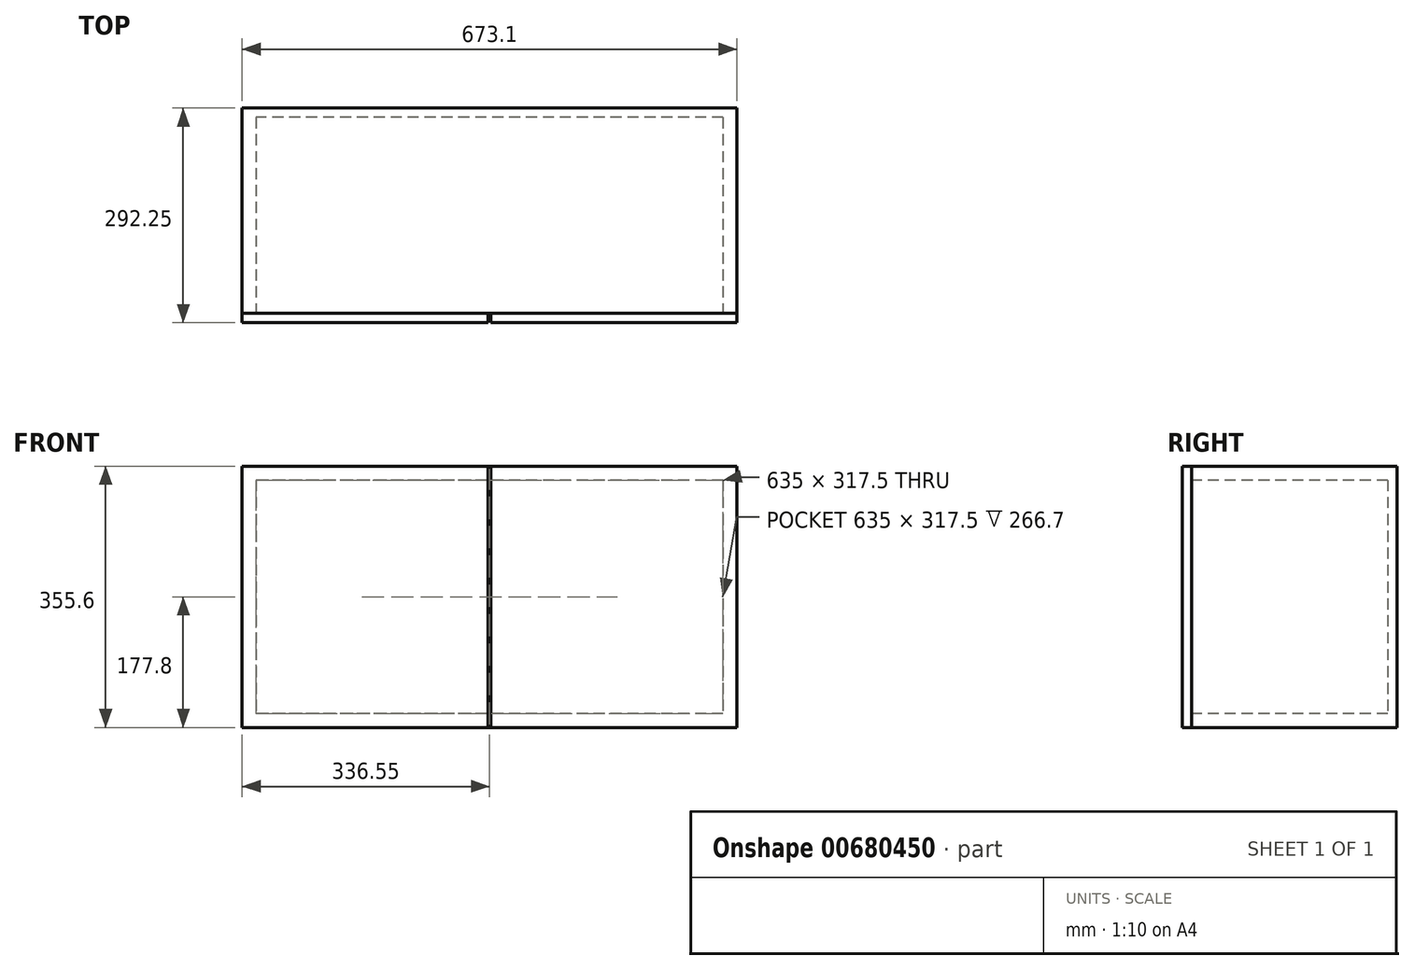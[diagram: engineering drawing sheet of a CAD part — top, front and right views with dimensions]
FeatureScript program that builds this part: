
annotation { "Feature Type Name" : "Feature", "Feature Type Description" : "" }
export const myFeature = defineFeature(function(context is Context, id is Id, definition is map)
    precondition{}
    {
        {
            var Q0;
            Q0=qCreatedBy(makeId("Front.planeOp"),FACE);
            var sketch = newSketch(context, id + "F0", { "sketchPlane" : qUnion([Q0])});
            skLineSegment(sketch, "E0.bottom", {"start": v(-336.55, 177.8) * mm, "end": v(336.55, 177.8) * mm});
            skLineSegment(sketch, "E0.top", {"start": v(-336.55, -177.8) * mm, "end": v(336.55, -177.8) * mm});
            skLineSegment(sketch, "E0.left", {"start": v(-336.55, 177.8) * mm, "end": v(-336.55, -177.8) * mm});
            skLineSegment(sketch, "E0.right", {"start": v(336.55, 177.8) * mm, "end": v(336.55, -177.8) * mm});
            skPoint(sketch, "E0.middle", {"position": v(0, 0) * mm});
            skSolve(sketch);
        }
        {
            var Q0;
            Q0=makeQuery(id+"F0.imprint","IMPRINT",FACE,{"disambiguationData":[TD([[makeQuery(id+"F0.imprint","IMPRINT",EDGE,{"derivedFrom":sQuery(id+"F0.wireOp",EDGE,"E0.bottom")}),-1.0]])]});
            extrude(context, id + "F1", {"entities" : qUnion([Q0]), "endBound" : BoundingType.SYMMETRIC, "depth" : 279.4 * mm});
        }
        {
            var Q0;
            Q0=makeQuery(id+"F1.opExtrude","CAP_FACE",FACE,{"disambiguationData":[OSD([sQuery(id+"F0.wireOp",EDGE,"E0.bottom"),sQuery(id+"F0.wireOp",EDGE,"E0.top"),sQuery(id+"F0.wireOp",EDGE,"E0.left"),sQuery(id+"F0.wireOp",EDGE,"E0.right")])],"isStart":false});
            var sketch = newSketch(context, id + "F2", { "sketchPlane" : qUnion([Q0])});
            skLineSegment(sketch, "E1.bottom", {"start": v(317.5, 158.75) * mm, "end": v(-317.5, 158.75) * mm});
            skLineSegment(sketch, "E1.top", {"start": v(317.5, -158.75) * mm, "end": v(-317.5, -158.75) * mm});
            skLineSegment(sketch, "E1.left", {"start": v(317.5, 158.75) * mm, "end": v(317.5, -158.75) * mm});
            skLineSegment(sketch, "E1.right", {"start": v(-317.5, 158.75) * mm, "end": v(-317.5, -158.75) * mm});
            skPoint(sketch, "E1.middle", {"position": v(0, 0) * mm});
            skSolve(sketch);
        }
        {
            var Q0;
            Q0=qSketchRegion(id+"F2",true);
            var Q1;
            Q1=makeQuery(id+"F1.opExtrude","CAP_FACE",FACE,{"disambiguationData":[OSD([sQuery(id+"F0.wireOp",EDGE,"E0.bottom"),sQuery(id+"F0.wireOp",EDGE,"E0.top"),sQuery(id+"F0.wireOp",EDGE,"E0.left"),sQuery(id+"F0.wireOp",EDGE,"E0.right")])],"isStart":true});
            extrude(context, id + "F3", {"entities" : qUnion([Q0]), "operationType" : NewBodyOperationType.REMOVE, "oppositeDirection" : true, "endBoundEntityFace" : qUnion([Q1]), "depth" : 266.7 * mm});
        }
        {
            var Q0;
            Q0=makeQuery(id+"F1.opExtrude","CAP_FACE",FACE,{"disambiguationData":[OSD([sQuery(id+"F0.wireOp",EDGE,"E0.bottom"),sQuery(id+"F0.wireOp",EDGE,"E0.top"),sQuery(id+"F0.wireOp",EDGE,"E0.left"),sQuery(id+"F0.wireOp",EDGE,"E0.right")])],"isStart":false});
            cPlane(context, id + "F4", {"entities" : qUnion([Q0]), "cplaneType" : CPlaneType.OFFSET, "offset" : .15 * mm, "width" : 150 * mm, "height" : 150 * mm});
        }
        {
            var Q0;
            Q0=qCreatedBy(id+"F4.planeOp",FACE);
            var sketch = newSketch(context, id + "F5", { "sketchPlane" : qUnion([Q0])});
            skLineSegment(sketch, "E2.bottom", {"start": v(-336.55, -177.8) * mm, "end": v(-1.9, -177.8) * mm});
            skLineSegment(sketch, "E2.top", {"start": v(-336.55, 177.8) * mm, "end": v(-1.9, 177.8) * mm});
            skLineSegment(sketch, "E2.left", {"start": v(-336.55, -177.8) * mm, "end": v(-336.55, 177.8) * mm});
            skLineSegment(sketch, "E2.right", {"start": v(-1.9, -177.8) * mm, "end": v(-1.9, 177.8) * mm});
            skSolve(sketch);
        }
        {
            var Q0;
            Q0=makeQuery(id+"F5.imprint","IMPRINT",FACE,{"disambiguationData":[TD([[makeQuery(id+"F5.imprint","IMPRINT",EDGE,{"derivedFrom":sQuery(id+"F5.wireOp",EDGE,"E2.bottom")}),1.0]])]});
            extrude(context, id + "F6", {"entities" : qUnion([Q0]), "depth" : 12.7 * mm});
        }
        {
            var Q0;
            Q0=makeQuery(id+"F6.opExtrude","SWEPT_BODY",BODY,{"disambiguationData":[OSD([sQuery(id+"F5.wireOp",EDGE,"E2.bottom"),sQuery(id+"F5.wireOp",EDGE,"E2.top"),sQuery(id+"F5.wireOp",EDGE,"E2.left"),sQuery(id+"F5.wireOp",EDGE,"E2.right")])]});
            var Q1;
            Q1=qCreatedBy(makeId("Right.planeOp"),FACE);
            mirror(context, id + "F7", {"entities" : qUnion([Q0]), "mirrorPlane" : qUnion([Q1])});
        }
    });
